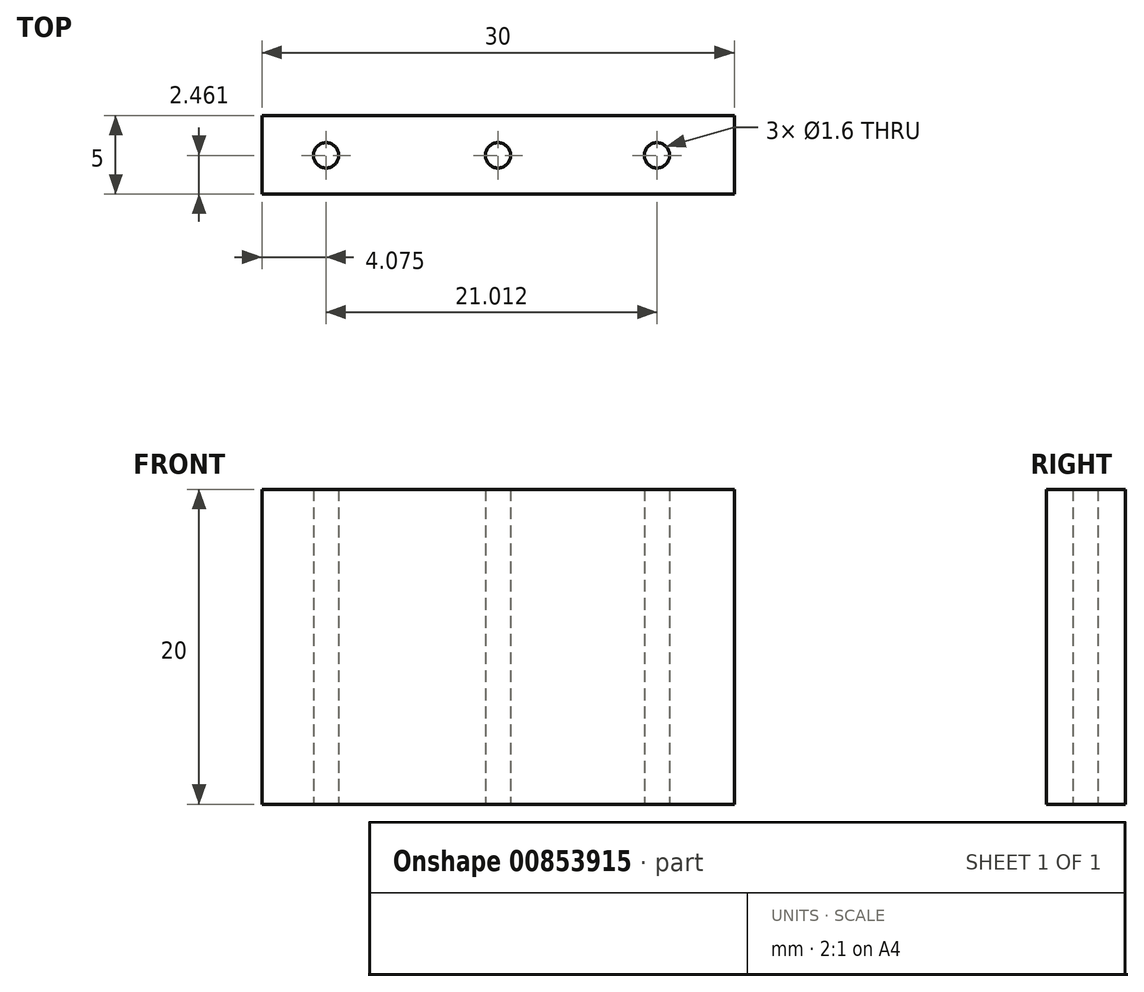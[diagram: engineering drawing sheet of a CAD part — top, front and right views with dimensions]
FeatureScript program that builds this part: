
annotation { "Feature Type Name" : "Feature", "Feature Type Description" : "" }
export const myFeature = defineFeature(function(context is Context, id is Id, definition is map)
    precondition{}
    {
        {
            var Q0;
            Q0=qCreatedBy(makeId("Top.planeOp"),FACE);
            var sketch = newSketch(context, id + "F0", { "sketchPlane" : qUnion([Q0])});
            skLineSegment(sketch, "E0.bottom", {"start": v(-14, 14.53) * mm, "end": v(16, 14.53) * mm});
            skLineSegment(sketch, "E0.top", {"start": v(-14, 9.53) * mm, "end": v(16, 9.53) * mm});
            skLineSegment(sketch, "E0.left", {"start": v(-14, 14.53) * mm, "end": v(-14, 9.53) * mm});
            skLineSegment(sketch, "E0.right", {"start": v(16, 14.53) * mm, "end": v(16, 9.53) * mm});
            skCircle(sketch, "E1", {"center": v(1, 12) * mm, "radius": 0.8 * mm});
            skCircle(sketch, "E2", {"center": v(-9.92, 12) * mm, "radius": 0.8 * mm});
            skCircle(sketch, "E3", {"center": v(11.09, 12) * mm, "radius": 0.8 * mm});
            skSolve(sketch);
        }
        {
            var Q0;
            Q0=makeQuery(id+"F0.imprint","IMPRINT",FACE,{"disambiguationData":[TD([[makeQuery(id+"F0.imprint","IMPRINT",EDGE,{"derivedFrom":sQuery(id+"F0.wireOp",EDGE,"E0.bottom")}),-1.0]])]});
            extrude(context, id + "F1", {"entities" : qUnion([Q0]), "depth" : 20 * mm, "offsetDistance" : 25.4 * mm});
        }
    });
